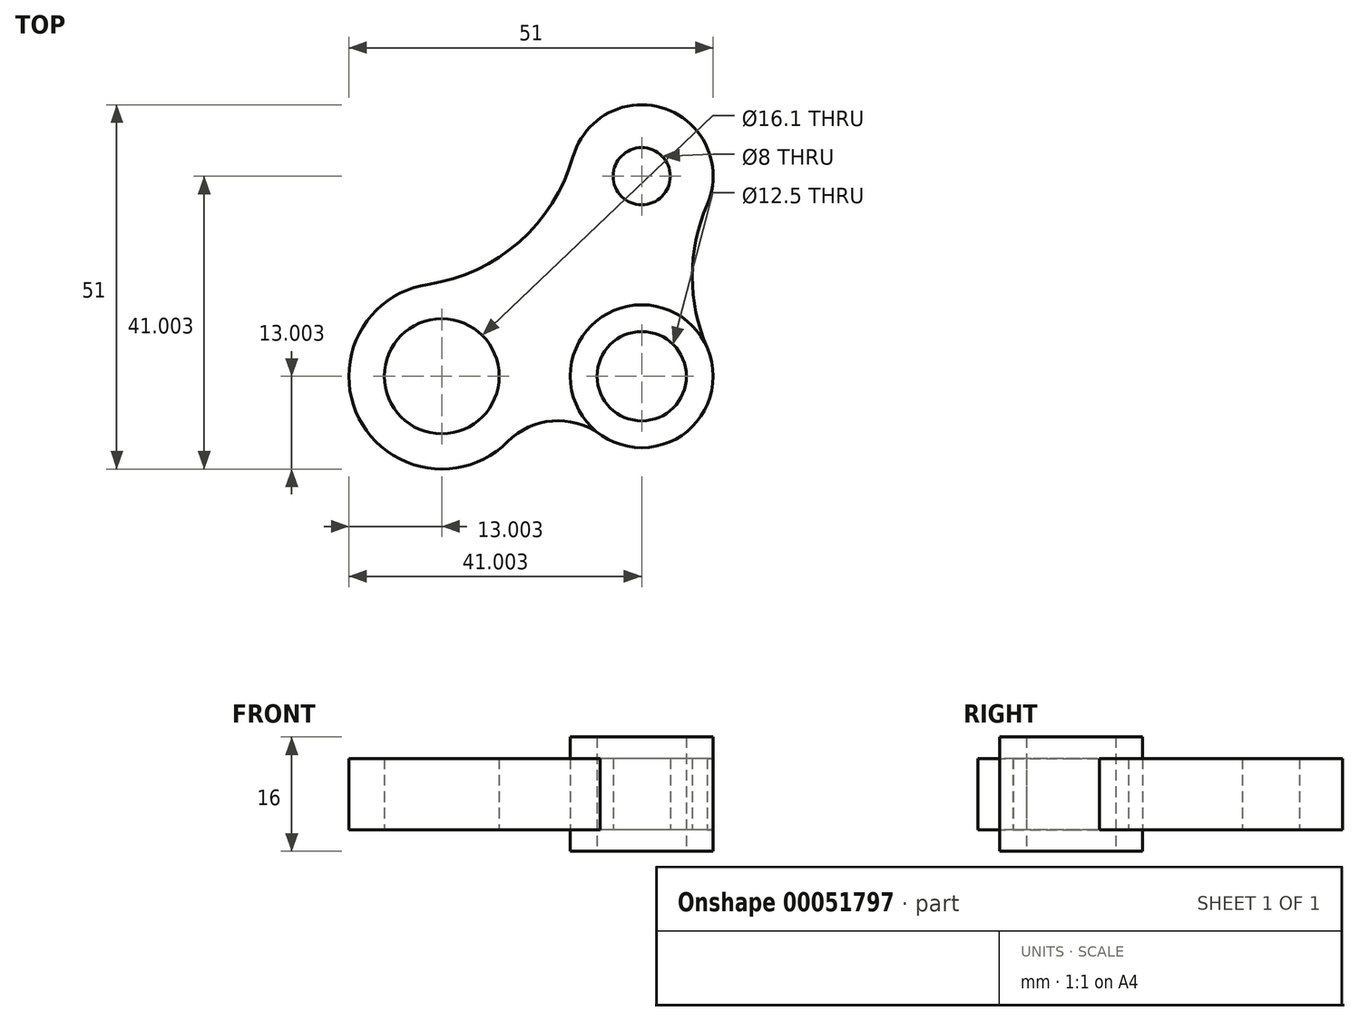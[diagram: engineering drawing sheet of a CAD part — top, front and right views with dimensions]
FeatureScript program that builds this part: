
annotation { "Feature Type Name" : "Feature", "Feature Type Description" : "" }
export const myFeature = defineFeature(function(context is Context, id is Id, definition is map)
    precondition{}
    {
        {
            var Q0;
            Q0=qCreatedBy(makeId("Top.planeOp"),FACE);
            var sketch = newSketch(context, id + "F0", { "sketchPlane" : qUnion([Q0])});
            skCircle(sketch, "E0", {"center": v(-51.2, 16.22) * mm, "radius": 8.05 * mm});
            skCircle(sketch, "E1", {"center": v(-23.2, 16.22) * mm, "radius": 6.25 * mm});
            skCircle(sketch, "E2", {"center": v(-23.2, 44.22) * mm, "radius": 10 * mm});
            skCircle(sketch, "E3", {"center": v(-23.2, 44.22) * mm, "radius": 4 * mm});
            skCircle(sketch, "E4", {"center": v(-51.2, 16.22) * mm, "radius": 13 * mm});
            skCircle(sketch, "E5", {"center": v(-23.2, 16.22) * mm, "radius": 10 * mm});
            skCircle(sketch, "E6", {"center": v(-23.2, 16.22) * mm, "radius": 28 * mm, "construction": true});
            skLineSegment(sketch, "E7", {"start": v(-23.2, 16.22) * mm, "end": v(-23.2, 64.87) * mm, "construction": true});
            skLineSegment(sketch, "E8", {"start": v(-23.2, 16.22) * mm, "end": v(-73.3, 16.22) * mm, "construction": true});
            skCircle(sketch, "E9", {"center": v(-34.9, 0) * mm, "radius": 10 * mm});
            skCircle(sketch, "E10", {"center": v(8.87, 30.22) * mm, "radius": 25 * mm});
            skCircle(sketch, "E11", {"center": v(-56.87, 53.8) * mm, "radius": 25 * mm});
            skSolve(sketch);
        }
        {
            var Q0;
            Q0=makeQuery(id+"F0.imprint","IMPRINT",FACE,{"disambiguationData":[TD([[makeQuery(id+"F0.imprint","IMPRINT",EDGE,{"derivedFrom":sQuery(id+"F0.wireOp",EDGE,"E1")}),-1.0]])]});
            extrude(context, id + "F1", {"entities" : qUnion([Q0]), "endBound" : BoundingType.SYMMETRIC, "depth" : 16 * mm});
        }
        {
            var Q0;
            {var subQ5=sQuery(id+"F0.wireOp",EDGE,"E10");var subQ6=sQuery(id+"F0.wireOp",EDGE,"E2");var subQ7=makeQuery(id+"F0.imprint","INTERSECT",VERTEX,{"derivedFrom":[subQ6,subQ5]});Q0=makeQuery(id+"F0.imprint","IMPRINT",FACE,{"disambiguationData":[TD([[makeQuery(id+"F0.imprint","IMPRINT",EDGE,{"disambiguationData":[TD([[subQ7,1.0]])],"derivedFrom":subQ6}),-1.0]])]});}
            var Q1;
            Q1=makeQuery(id+"F0.imprint","IMPRINT",FACE,{"disambiguationData":[TD([[makeQuery(id+"F0.imprint","IMPRINT",EDGE,{"derivedFrom":sQuery(id+"F0.wireOp",EDGE,"E3")}),-1.0]])]});
            var Q2;
            Q2=makeQuery(id+"F0.imprint","IMPRINT",FACE,{"disambiguationData":[TD([[makeQuery(id+"F0.imprint","IMPRINT",EDGE,{"derivedFrom":sQuery(id+"F0.wireOp",EDGE,"E0")}),-1.0]])]});
            extrude(context, id + "F2", {"entities" : qUnion([Q0, Q1, Q2]), "endBound" : BoundingType.SYMMETRIC, "depth" : 10 * mm});
        }
    });
